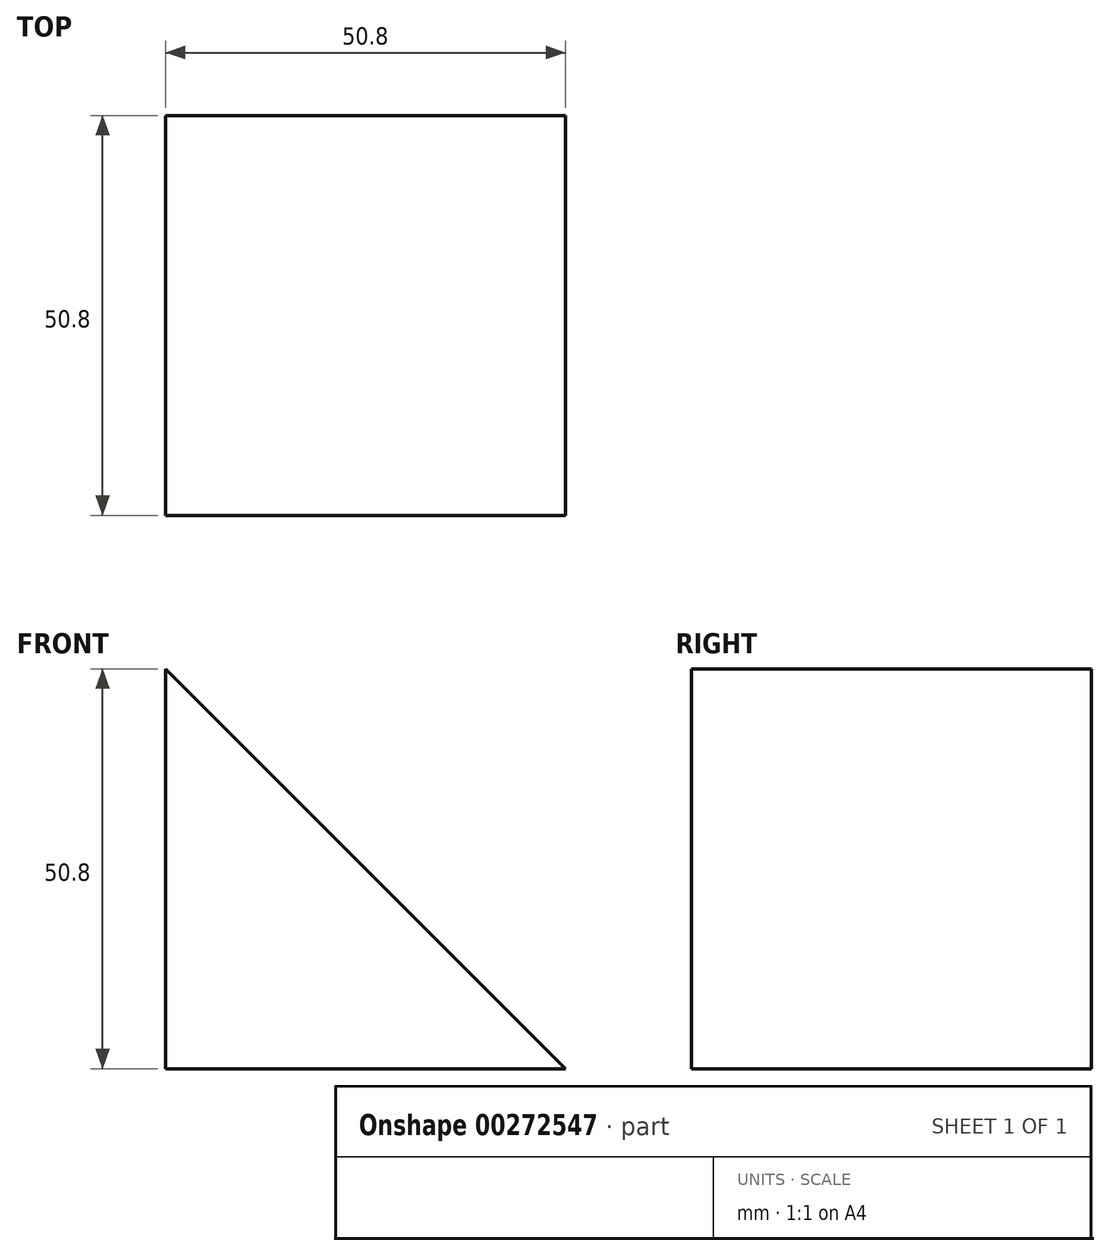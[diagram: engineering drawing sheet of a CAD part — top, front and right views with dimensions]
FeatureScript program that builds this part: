
annotation { "Feature Type Name" : "Feature", "Feature Type Description" : "" }
export const myFeature = defineFeature(function(context is Context, id is Id, definition is map)
    precondition{}
    {
        {
            var Q0;
            Q0=qCreatedBy(makeId("Front.planeOp"),FACE);
            var sketch = newSketch(context, id + "F0", { "sketchPlane" : qUnion([Q0])});
            skLineSegment(sketch, "E0", {"start": v(0, 0) * mm, "end": v(-50.8, 0) * mm});
            skLineSegment(sketch, "E1", {"start": v(-50.8, 0) * mm, "end": v(-50.8, 50.8) * mm});
            skLineSegment(sketch, "E2", {"start": v(-50.8, 50.8) * mm, "end": v(0, 0) * mm});
            skSolve(sketch);
        }
        {
            var Q0;
            Q0=makeQuery(id+"F0.imprint","IMPRINT",FACE,{"disambiguationData":[TD([[makeQuery(id+"F0.imprint","IMPRINT",EDGE,{"derivedFrom":sQuery(id+"F0.wireOp",EDGE,"E0")}),-1.0]])]});
            extrude(context, id + "F1", {"entities" : qUnion([Q0]), "depth" : 50.8 * mm});
        }
    });
